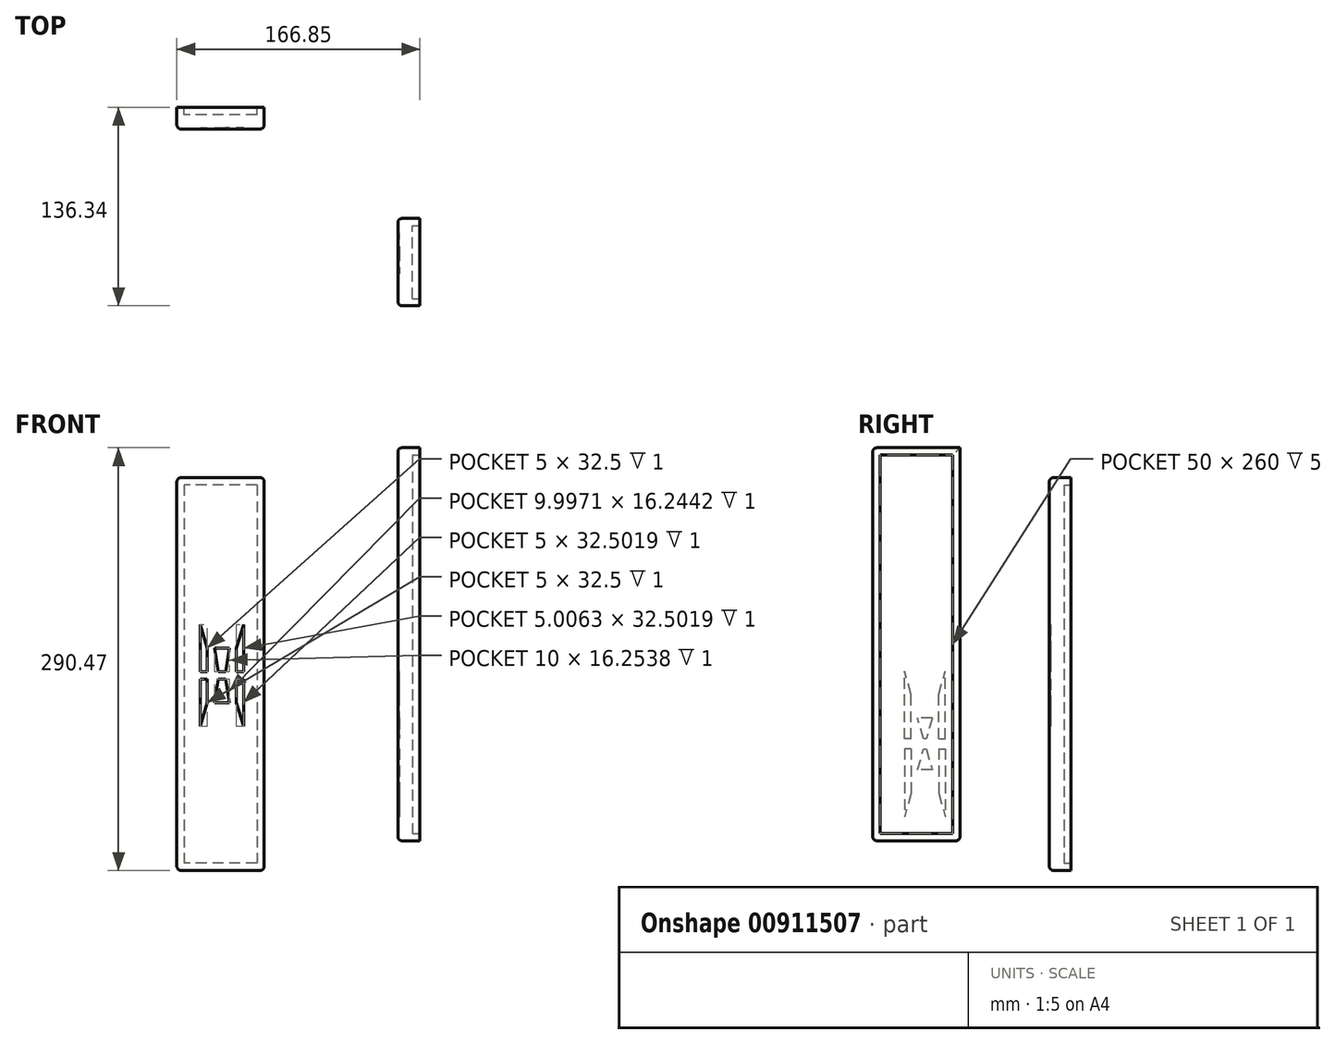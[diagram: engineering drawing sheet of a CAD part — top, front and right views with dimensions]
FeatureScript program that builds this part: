
annotation { "Feature Type Name" : "Feature", "Feature Type Description" : "" }
export const myFeature = defineFeature(function(context is Context, id is Id, definition is map)
    precondition{}
    {
        {
            var Q0;
            Q0=qCreatedBy(makeId("Front.planeOp"),FACE);
            var sketch = newSketch(context, id + "F0", { "sketchPlane" : qUnion([Q0])});
            skPoint(sketch, "E0.middle", {"position": v(0, 0) * mm});
            skLineSegment(sketch, "E1.bottom", {"start": v(-151.85, 109.1) * mm, "end": v(-91.85, 109.1) * mm});
            skLineSegment(sketch, "E1.top", {"start": v(-151.85, -160.9) * mm, "end": v(-91.85, -160.9) * mm});
            skLineSegment(sketch, "E1.left", {"start": v(-151.85, 109.1) * mm, "end": v(-151.85, -160.9) * mm});
            skLineSegment(sketch, "E1.right", {"start": v(-91.85, 109.1) * mm, "end": v(-91.85, -160.9) * mm});
            skSolve(sketch);
        }
        {
            var Q0;
            Q0=qCreatedBy(makeId("Right.planeOp"),FACE);
            var sketch = newSketch(context, id + "F1", { "sketchPlane" : qUnion([Q0])});
            skLineSegment(sketch, "E2.bottom", {"start": v(-136.34, 129.58) * mm, "end": v(-76.34, 129.58) * mm});
            skLineSegment(sketch, "E2.top", {"start": v(-136.34, -140.42) * mm, "end": v(-76.34, -140.42) * mm});
            skLineSegment(sketch, "E2.left", {"start": v(-136.34, 129.58) * mm, "end": v(-136.34, -140.42) * mm});
            skLineSegment(sketch, "E2.right", {"start": v(-76.34, 129.58) * mm, "end": v(-76.34, -140.42) * mm});
            skSolve(sketch);
        }
        {
            var Q0;
            Q0=qSketchRegion(id+"F0",true);
            extrude(context, id + "F2", {"entities" : qUnion([Q0]), "depth" : 15 * mm, "offsetDistance" : 25 * mm});
        }
        {
            var Q0;
            Q0=makeQuery(id+"F0.imprint","IMPRINT",FACE,{"disambiguationData":[TD([[makeQuery(id+"F0.imprint","IMPRINT",EDGE,{"derivedFrom":sQuery(id+"F0.wireOp",EDGE,"E1.bottom")}),-1.0]])]});
            var sketch = newSketch(context, id + "F3", { "sketchPlane" : qUnion([Q0])});
            skLineSegment(sketch, "E3.bottom", {"start": v(-96.85, 104.1) * mm, "end": v(-146.85, 104.1) * mm});
            skLineSegment(sketch, "E3.top", {"start": v(-96.85, -155.9) * mm, "end": v(-146.85, -155.9) * mm});
            skLineSegment(sketch, "E3.left", {"start": v(-96.85, 104.1) * mm, "end": v(-96.85, -155.9) * mm});
            skLineSegment(sketch, "E3.right", {"start": v(-146.85, 104.1) * mm, "end": v(-146.85, -155.9) * mm});
            skSolve(sketch);
        }
        {
            var Q0;
            Q0=makeQuery(id+"F3.imprint","IMPRINT",FACE,{"disambiguationData":[TD([[makeQuery(id+"F3.imprint","IMPRINT",EDGE,{"derivedFrom":sQuery(id+"F3.wireOp",EDGE,"E3.bottom")}),1.0]])]});
            extrude(context, id + "F4", {"entities" : qUnion([Q0]), "operationType" : NewBodyOperationType.ADD, "depth" : -5 * mm, "offsetDistance" : 25 * mm});
        }
        {
            var Q0;
            Q0=qSketchRegion(id+"F1",true);
            extrude(context, id + "F5", {"entities" : qUnion([Q0]), "depth" : 15 * mm, "offsetDistance" : 25 * mm});
        }
        {
            var Q0;
            Q0=makeQuery(id+"F5.opExtrude","CAP_FACE",FACE,{"disambiguationData":[OSD([sQuery(id+"F1.wireOp",EDGE,"E2.bottom"),sQuery(id+"F1.wireOp",EDGE,"E2.top"),sQuery(id+"F1.wireOp",EDGE,"E2.left"),sQuery(id+"F1.wireOp",EDGE,"E2.right")])],"isStart":false});
            var sketch = newSketch(context, id + "F6", { "sketchPlane" : qUnion([Q0])});
            skLineSegment(sketch, "E4.bottom", {"start": v(-131.34, 124.58) * mm, "end": v(-81.34, 124.58) * mm});
            skLineSegment(sketch, "E4.top", {"start": v(-131.34, -135.42) * mm, "end": v(-81.34, -135.42) * mm});
            skLineSegment(sketch, "E4.left", {"start": v(-131.34, 124.58) * mm, "end": v(-131.34, -135.42) * mm});
            skLineSegment(sketch, "E4.right", {"start": v(-81.34, 124.58) * mm, "end": v(-81.34, -135.42) * mm});
            skSolve(sketch);
        }
        {
            var Q0;
            Q0=makeQuery(id+"F6.imprint","IMPRINT",FACE,{"disambiguationData":[TD([[makeQuery(id+"F6.imprint","IMPRINT",EDGE,{"derivedFrom":sQuery(id+"F6.wireOp",EDGE,"E4.bottom")}),-1.0]])]});
            extrude(context, id + "F7", {"entities" : qUnion([Q0]), "operationType" : NewBodyOperationType.REMOVE, "oppositeDirection" : true, "depth" : 5 * mm, "offsetDistance" : 25 * mm});
        }
        {
            var Q0;
            Q0=makeQuery(id+"F4.opExtrude","CAP_FACE",FACE,{"disambiguationData":[OSD([sQuery(id+"F3.wireOp",EDGE,"E3.bottom"),sQuery(id+"F3.wireOp",EDGE,"E3.top"),sQuery(id+"F3.wireOp",EDGE,"E3.left"),sQuery(id+"F3.wireOp",EDGE,"E3.right")])],"isStart":false});
            var sketch = newSketch(context, id + "F8", { "sketchPlane" : qUnion([Q0])});
            skLineSegment(sketch, "E5.bottom", {"start": v(133.85, -150.9) * mm, "end": v(109.85, -150.9) * mm});
            skLineSegment(sketch, "E5.top", {"start": v(133.85, 99.1) * mm, "end": v(109.85, 99.1) * mm});
            skLineSegment(sketch, "E5.left", {"start": v(133.85, -150.9) * mm, "end": v(133.85, 99.1) * mm});
            skLineSegment(sketch, "E5.right", {"start": v(109.85, -150.9) * mm, "end": v(109.85, 99.1) * mm});
            skEllipse(sketch, "E6", {"center": v(121.85, -25.9) * mm, "majorRadius": 25 * mm, "minorRadius": 20 * mm, "majorAxis": v(0, 1)});
            skSolve(sketch);
        }
        {
            var Q0;
            Q0=makeQuery(id+"F8.imprint","IMPRINT",FACE,{"disambiguationData":[TD([[makeQuery(id+"F8.imprint","IMPRINT",EDGE,{"derivedFrom":sQuery(id+"F8.wireOp",EDGE,"E5.bottom")}),-1.0]])]});
            var Q1;
            {var subQ0=sQuery(id+"F8.wireOp",EDGE,"E5.right");var subQ1=sQuery(id+"F8.wireOp",EDGE,"E5.top");var subQ2=makeQuery(id+"F8.imprint","INTERSECT",VERTEX,{"derivedFrom":[subQ1,subQ0]});Q1=makeQuery(id+"F8.imprint","IMPRINT",FACE,{"disambiguationData":[TD([[makeQuery(id+"F8.imprint","IMPRINT",EDGE,{"disambiguationData":[TD([[subQ2,1.0]])],"derivedFrom":subQ1}),1.0]])]});}
            var Q2;
            {var subQ0=sQuery(id+"F8.wireOp",EDGE,"E5.left");var subQ1=sQuery(id+"F8.wireOp",EDGE,"E5.top");var subQ2=makeQuery(id+"F8.imprint","INTERSECT",VERTEX,{"derivedFrom":[subQ1,subQ0]});Q2=makeQuery(id+"F8.imprint","IMPRINT",FACE,{"disambiguationData":[TD([[makeQuery(id+"F8.imprint","IMPRINT",EDGE,{"disambiguationData":[TD([[subQ2,-1.0]])],"derivedFrom":subQ1}),1.0]])]});}
            var Q3;
            {var subQ0=sQuery(id+"F8.wireOp",EDGE,"jjR4p86R-AGvj-MJNc-cVGU-iWlVXVb1kiAX");var subQ1=sQuery(id+"F8.wireOp",EDGE,"E5.right");var subQ2=makeQuery(id+"F8.imprint","INTERSECT",VERTEX,{"derivedFrom":[subQ1,subQ0]});Q3=makeQuery(id+"F8.imprint","IMPRINT",FACE,{"disambiguationData":[TD([[makeQuery(id+"F8.imprint","IMPRINT",EDGE,{"disambiguationData":[TD([[subQ2,-1.0]])],"derivedFrom":subQ1}),-1.0]])]});}
            var Q4;
            {var subQ0=sQuery(id+"F8.wireOp",EDGE,"jjR4p86R-AGvj-MJNc-cVGU-iWlVXVb1kiAX");var subQ1=sQuery(id+"F8.wireOp",EDGE,"E5.left");var subQ2=makeQuery(id+"F8.imprint","INTERSECT",VERTEX,{"derivedFrom":[subQ1,subQ0]});Q4=makeQuery(id+"F8.imprint","IMPRINT",FACE,{"disambiguationData":[TD([[makeQuery(id+"F8.imprint","IMPRINT",EDGE,{"disambiguationData":[TD([[subQ2,-1.0]])],"derivedFrom":subQ1}),1.0]])]});}
            var Q5;
            {var subQ0=sQuery(id+"F8.wireOp",EDGE,"jjR4p86R-AGvj-MJNc-cVGU-iWlVXVb1kiAX");var subQ1=sQuery(id+"F8.wireOp",EDGE,"E5.left");var subQ2=makeQuery(id+"F8.imprint","INTERSECT",VERTEX,{"derivedFrom":[subQ1,subQ0]});Q5=makeQuery(id+"F8.imprint","IMPRINT",FACE,{"disambiguationData":[TD([[makeQuery(id+"F8.imprint","IMPRINT",EDGE,{"disambiguationData":[TD([[subQ2,-1.0]])],"derivedFrom":subQ1}),-1.0]])]});}
            var Q6;
            {var subQ0=sQuery(id+"F8.wireOp",EDGE,"E6");var subQ1=sQuery(id+"F8.wireOp",EDGE,"E5.left");var subQ2=makeQuery(id+"F8.imprint","INTERSECT",VERTEX,{"disambiguationData":[OD(0.0)],"derivedFrom":[subQ1,subQ0]});Q6=makeQuery(id+"F8.imprint","IMPRINT",FACE,{"disambiguationData":[TD([[makeQuery(id+"F8.imprint","IMPRINT",EDGE,{"disambiguationData":[TD([[subQ2,-1.0]])],"derivedFrom":subQ1}),-1.0]])]});}
            var Q7;
            {var subQ0=sQuery(id+"F8.wireOp",EDGE,"E6");var subQ1=sQuery(id+"F8.wireOp",EDGE,"E5.left");var subQ2=makeQuery(id+"F8.imprint","INTERSECT",VERTEX,{"disambiguationData":[OD(0.0)],"derivedFrom":[subQ1,subQ0]});Q7=makeQuery(id+"F8.imprint","IMPRINT",FACE,{"disambiguationData":[TD([[makeQuery(id+"F8.imprint","IMPRINT",EDGE,{"disambiguationData":[TD([[subQ2,-1.0]])],"derivedFrom":subQ1}),1.0]])]});}
            var Q8;
            {var subQ0=sQuery(id+"F8.wireOp",EDGE,"E6");var subQ1=sQuery(id+"F8.wireOp",EDGE,"E5.right");var subQ2=makeQuery(id+"F8.imprint","INTERSECT",VERTEX,{"disambiguationData":[OD(0.0)],"derivedFrom":[subQ1,subQ0]});Q8=makeQuery(id+"F8.imprint","IMPRINT",FACE,{"disambiguationData":[TD([[makeQuery(id+"F8.imprint","IMPRINT",EDGE,{"disambiguationData":[TD([[subQ2,-1.0]])],"derivedFrom":subQ1}),-1.0]])]});}
            var Q9;
            {var subQ0=sQuery(id+"F8.wireOp",EDGE,"E6");var subQ1=sQuery(id+"F8.wireOp",EDGE,"E5.right");var subQ2=makeQuery(id+"F8.imprint","INTERSECT",VERTEX,{"disambiguationData":[OD(0.0)],"derivedFrom":[subQ1,subQ0]});Q9=makeQuery(id+"F8.imprint","IMPRINT",FACE,{"disambiguationData":[TD([[makeQuery(id+"F8.imprint","IMPRINT",EDGE,{"disambiguationData":[TD([[subQ2,-1.0]])],"derivedFrom":subQ1}),1.0]])]});}
            var Q10;
            {var subQ0=sQuery(id+"F8.wireOp",EDGE,"jjR4p86R-AGvj-MJNc-cVGU-iWlVXVb1kiAX");var subQ1=sQuery(id+"F8.wireOp",EDGE,"E5.right");var subQ2=makeQuery(id+"F8.imprint","INTERSECT",VERTEX,{"derivedFrom":[subQ1,subQ0]});Q10=makeQuery(id+"F8.imprint","IMPRINT",FACE,{"disambiguationData":[TD([[makeQuery(id+"F8.imprint","IMPRINT",EDGE,{"disambiguationData":[TD([[subQ2,-1.0]])],"derivedFrom":subQ1}),1.0]])]});}
            extrude(context, id + "F9", {"entities" : qUnion([Q0, Q1, Q2, Q3, Q4, Q5, Q6, Q7, Q8, Q9, Q10]), "operationType" : NewBodyOperationType.REMOVE, "oppositeDirection" : true, "depth" : 10 * mm, "offsetDistance" : 25 * mm});
        }
        {
            var Q0;
            Q0=makeQuery(id+"F2.opExtrude","CAP_EDGE",EDGE,{"disambiguationData":[OSD([sQuery(id+"F0.wireOp",EDGE,"E1.bottom")])],"isStart":false});
            var Q1;
            Q1=makeQuery(id+"F2.opExtrude","SWEPT_EDGE",EDGE,{"disambiguationData":[OSD([sQuery(id+"F0.wireOp",EDGE,"E1.bottom"),sQuery(id+"F0.wireOp",EDGE,"E1.left")])]});
            var Q2;
            Q2=makeQuery(id+"F2.opExtrude","SWEPT_EDGE",EDGE,{"disambiguationData":[OSD([sQuery(id+"F0.wireOp",EDGE,"E1.bottom"),sQuery(id+"F0.wireOp",EDGE,"E1.right")])]});
            var Q3;
            Q3=makeQuery(id+"F2.opExtrude","CAP_EDGE",EDGE,{"disambiguationData":[OSD([sQuery(id+"F0.wireOp",EDGE,"E1.right")])],"isStart":false});
            var Q4;
            Q4=makeQuery(id+"F2.opExtrude","CAP_EDGE",EDGE,{"disambiguationData":[OSD([sQuery(id+"F0.wireOp",EDGE,"E1.left")])],"isStart":false});
            var Q5;
            Q5=makeQuery(id+"F2.opExtrude","CAP_EDGE",EDGE,{"disambiguationData":[OSD([sQuery(id+"F0.wireOp",EDGE,"E1.top")])],"isStart":false});
            var Q6;
            Q6=makeQuery(id+"F2.opExtrude","SWEPT_EDGE",EDGE,{"disambiguationData":[OSD([sQuery(id+"F0.wireOp",EDGE,"E1.top"),sQuery(id+"F0.wireOp",EDGE,"E1.left")])]});
            var Q7;
            Q7=makeQuery(id+"F2.opExtrude","SWEPT_EDGE",EDGE,{"disambiguationData":[OSD([sQuery(id+"F0.wireOp",EDGE,"E1.top"),sQuery(id+"F0.wireOp",EDGE,"E1.right")])]});
            fillet(context, id + "F10", {"entities" : qUnion([Q0, Q1, Q2, Q3, Q4, Q5, Q6, Q7]), "radius" : 3 * mm, "tangentPropagation" : true, "allowEdgeOverflow" : false});
        }
        {
            var Q0;
            Q0=makeQuery(id+"F5.opExtrude","SWEPT_EDGE",EDGE,{"disambiguationData":[OSD([sQuery(id+"F1.wireOp",EDGE,"E2.bottom"),sQuery(id+"F1.wireOp",EDGE,"E2.left")])]});
            var Q1;
            Q1=makeQuery(id+"F5.opExtrude","CAP_EDGE",EDGE,{"disambiguationData":[OSD([sQuery(id+"F1.wireOp",EDGE,"E2.bottom")])],"isStart":true});
            var Q2;
            Q2=makeQuery(id+"F5.opExtrude","CAP_EDGE",EDGE,{"disambiguationData":[OSD([sQuery(id+"F1.wireOp",EDGE,"E2.left")])],"isStart":true});
            var Q3;
            Q3=makeQuery(id+"F5.opExtrude","CAP_EDGE",EDGE,{"disambiguationData":[OSD([sQuery(id+"F1.wireOp",EDGE,"E2.right")])],"isStart":true});
            var Q4;
            Q4=makeQuery(id+"F5.opExtrude","CAP_EDGE",EDGE,{"disambiguationData":[OSD([sQuery(id+"F1.wireOp",EDGE,"E2.top")])],"isStart":true});
            var Q5;
            Q5=makeQuery(id+"F5.opExtrude","SWEPT_EDGE",EDGE,{"disambiguationData":[OSD([sQuery(id+"F1.wireOp",EDGE,"E2.top"),sQuery(id+"F1.wireOp",EDGE,"E2.right")])]});
            var Q6;
            Q6=makeQuery(id+"F5.opExtrude","SWEPT_EDGE",EDGE,{"disambiguationData":[OSD([sQuery(id+"F1.wireOp",EDGE,"E2.top"),sQuery(id+"F1.wireOp",EDGE,"E2.left")])]});
            fillet(context, id + "F11", {"entities" : qUnion([Q0, Q1, Q2, Q3, Q4, Q5, Q6]), "radius" : 3 * mm, "tangentPropagation" : true, "allowEdgeOverflow" : false});
        }
        {
            var Q0;
            Q0=makeQuery(id+"F5.opExtrude","CAP_FACE",FACE,{"disambiguationData":[OSD([sQuery(id+"F1.wireOp",EDGE,"E2.bottom"),sQuery(id+"F1.wireOp",EDGE,"E2.top"),sQuery(id+"F1.wireOp",EDGE,"E2.left"),sQuery(id+"F1.wireOp",EDGE,"E2.right")])],"isStart":true});
            var sketch = newSketch(context, id + "F12", { "sketchPlane" : qUnion([Q0])});
            skLineSegment(sketch, "E7", {"start": v(95.46, -56.01) * mm, "end": v(105.46, -56.01) * mm});
            skLineSegment(sketch, "E8", {"start": v(95.46, -91.72) * mm, "end": v(105.46, -91.72) * mm});
            skLineSegment(sketch, "E9", {"start": v(90.96, -39.94) * mm, "end": v(86.46, -23.87) * mm});
            skLineSegment(sketch, "E10", {"start": v(90.96, -107.8) * mm, "end": v(86.46, -123.87) * mm});
            skLineSegment(sketch, "E11", {"start": v(109.96, -107.8) * mm, "end": v(114.46, -123.87) * mm});
            skLineSegment(sketch, "E12", {"start": v(109.96, -39.94) * mm, "end": v(114.46, -23.87) * mm});
            skLineSegment(sketch, "E13", {"start": v(95.46, -56.01) * mm, "end": v(99.5, -70.46) * mm});
            skLineSegment(sketch, "E14", {"start": v(99.5, -70.46) * mm, "end": v(101.41, -70.46) * mm});
            skLineSegment(sketch, "E15", {"start": v(101.41, -70.46) * mm, "end": v(105.46, -56.01) * mm});
            skLineSegment(sketch, "E16", {"start": v(105.46, -91.72) * mm, "end": v(101.41, -77.27) * mm});
            skLineSegment(sketch, "E17", {"start": v(101.41, -77.27) * mm, "end": v(99.5, -77.27) * mm});
            skLineSegment(sketch, "E18", {"start": v(99.5, -77.27) * mm, "end": v(95.46, -91.72) * mm});
            skLineSegment(sketch, "E19", {"start": v(90.96, -77.27) * mm, "end": v(86.46, -77.27) * mm});
            skLineSegment(sketch, "E20", {"start": v(109.96, -77.27) * mm, "end": v(114.46, -77.27) * mm});
            skLineSegment(sketch, "E21", {"start": v(109.96, -70.46) * mm, "end": v(114.46, -70.46) * mm});
            skLineSegment(sketch, "E22", {"start": v(109.96, -70.46) * mm, "end": v(109.96, -39.94) * mm});
            skLineSegment(sketch, "E23", {"start": v(109.96, -77.27) * mm, "end": v(109.96, -107.8) * mm});
            skLineSegment(sketch, "E24", {"start": v(90.96, -70.46) * mm, "end": v(86.46, -70.46) * mm});
            skLineSegment(sketch, "E25", {"start": v(90.96, -70.46) * mm, "end": v(90.96, -39.94) * mm});
            skLineSegment(sketch, "E26", {"start": v(90.96, -77.27) * mm, "end": v(90.96, -107.8) * mm});
            skLineSegment(sketch, "E27", {"start": v(86.46, -70.46) * mm, "end": v(86.46, -23.87) * mm});
            skLineSegment(sketch, "E28", {"start": v(86.46, -77.27) * mm, "end": v(86.46, -123.87) * mm});
            skLineSegment(sketch, "E29", {"start": v(114.46, -70.46) * mm, "end": v(114.46, -23.87) * mm});
            skLineSegment(sketch, "E30", {"start": v(114.46, -77.27) * mm, "end": v(114.46, -123.87) * mm});
            skSolve(sketch);
        }
        {
            var Q0;
            Q0=makeQuery(id+"F12.imprint","IMPRINT",FACE,{"disambiguationData":[TD([[makeQuery(id+"F12.imprint","IMPRINT",EDGE,{"derivedFrom":sQuery(id+"F12.wireOp",EDGE,"E7")}),-1.0]])]});
            var Q1;
            Q1=makeQuery(id+"F12.imprint","IMPRINT",FACE,{"disambiguationData":[TD([[makeQuery(id+"F12.imprint","IMPRINT",EDGE,{"derivedFrom":sQuery(id+"F12.wireOp",EDGE,"E9")}),1.0]])]});
            var Q2;
            Q2=makeQuery(id+"F12.imprint","IMPRINT",FACE,{"disambiguationData":[TD([[makeQuery(id+"F12.imprint","IMPRINT",EDGE,{"derivedFrom":sQuery(id+"F12.wireOp",EDGE,"E12")}),-1.0]])]});
            var Q3;
            Q3=makeQuery(id+"F12.imprint","IMPRINT",FACE,{"disambiguationData":[TD([[makeQuery(id+"F12.imprint","IMPRINT",EDGE,{"derivedFrom":sQuery(id+"F12.wireOp",EDGE,"E11")}),1.0]])]});
            var Q4;
            Q4=makeQuery(id+"F12.imprint","IMPRINT",FACE,{"disambiguationData":[TD([[makeQuery(id+"F12.imprint","IMPRINT",EDGE,{"derivedFrom":sQuery(id+"F12.wireOp",EDGE,"E8")}),1.0]])]});
            var Q5;
            Q5=makeQuery(id+"F12.imprint","IMPRINT",FACE,{"disambiguationData":[TD([[makeQuery(id+"F12.imprint","IMPRINT",EDGE,{"derivedFrom":sQuery(id+"F12.wireOp",EDGE,"E10")}),-1.0]])]});
            extrude(context, id + "F13", {"entities" : qUnion([Q0, Q1, Q2, Q3, Q4, Q5]), "operationType" : NewBodyOperationType.REMOVE, "oppositeDirection" : true, "depth" : 1 * mm, "offsetDistance" : 25 * mm});
        }
        {
            var Q0;
            Q0=makeQuery(id+"F2.opExtrude","CAP_FACE",FACE,{"disambiguationData":[OSD([sQuery(id+"F0.wireOp",EDGE,"E1.bottom"),sQuery(id+"F0.wireOp",EDGE,"E1.top"),sQuery(id+"F0.wireOp",EDGE,"E1.left"),sQuery(id+"F0.wireOp",EDGE,"E1.right")])],"isStart":false});
            var sketch = newSketch(context, id + "F14", { "sketchPlane" : qUnion([Q0])});
            skLineSegment(sketch, "E31", {"start": v(-135.9, -24.37) * mm, "end": v(-130.9, -24.37) * mm});
            skLineSegment(sketch, "E32", {"start": v(-130.9, -24.37) * mm, "end": v(-130.9, -8.12) * mm});
            skLineSegment(sketch, "E33", {"start": v(-130.9, -8.12) * mm, "end": v(-135.9, 8.13) * mm});
            skLineSegment(sketch, "E34", {"start": v(-125.9, -8.12) * mm, "end": v(-120.9, -8.12) * mm});
            skLineSegment(sketch, "E35", {"start": v(-120.9, -8.12) * mm, "end": v(-115.9, -8.12) * mm});
            skLineSegment(sketch, "E36", {"start": v(-125.9, -8.12) * mm, "end": v(-115.9, -8.12) * mm});
            skLineSegment(sketch, "E37", {"start": v(-110.9, -8.12) * mm, "end": v(-110.9, -24.37) * mm});
            skLineSegment(sketch, "E38", {"start": v(-110.9, -24.37) * mm, "end": v(-105.9, -24.37) * mm});
            skLineSegment(sketch, "E39", {"start": v(-105.9, -24.37) * mm, "end": v(-105.9, 8.13) * mm});
            skLineSegment(sketch, "E40", {"start": v(-105.9, 8.13) * mm, "end": v(-110.9, -8.12) * mm});
            skLineSegment(sketch, "E41", {"start": v(-135.9, 8.13) * mm, "end": v(-135.9, -24.37) * mm});
            skLineSegment(sketch, "E42.MirrorCS", {"start": v(-110.9, -24.38) * mm, "end": v(-105.9, -24.38) * mm});
            skLineSegment(sketch, "E43", {"start": v(-135.9, -29.37) * mm, "end": v(-135.9, -61.87) * mm});
            skLineSegment(sketch, "E44", {"start": v(-135.9, -29.37) * mm, "end": v(-135.9, -45.62) * mm});
            skLineSegment(sketch, "E45", {"start": v(-135.9, -29.37) * mm, "end": v(-130.9, -29.37) * mm});
            skLineSegment(sketch, "E46", {"start": v(-130.9, -29.37) * mm, "end": v(-130.9, -45.62) * mm});
            skLineSegment(sketch, "E47", {"start": v(-130.9, -45.62) * mm, "end": v(-135.9, -61.87) * mm});
            skLineSegment(sketch, "E48", {"start": v(-110.9, -29.38) * mm, "end": v(-110.9, -45.63) * mm});
            skLineSegment(sketch, "E49", {"start": v(-105.9, -29.38) * mm, "end": v(-105.9, -61.88) * mm});
            skLineSegment(sketch, "E50", {"start": v(-105.9, -61.88) * mm, "end": v(-110.9, -45.63) * mm});
            skLineSegment(sketch, "E51", {"start": v(-125.9, -45.62) * mm, "end": v(-115.9, -45.62) * mm});
            skLineSegment(sketch, "E52", {"start": v(-110.9, -29.38) * mm, "end": v(-105.9, -29.38) * mm});
            skLineSegment(sketch, "E53", {"start": v(-123.4, -24.37) * mm, "end": v(-118.4, -24.37) * mm});
            skLineSegment(sketch, "E54", {"start": v(-125.9, -8.12) * mm, "end": v(-123.4, -24.37) * mm});
            skLineSegment(sketch, "E55", {"start": v(-115.9, -8.12) * mm, "end": v(-118.4, -24.37) * mm});
            skLineSegment(sketch, "E56.MirrorCS", {"start": v(-125.9, -45.63) * mm, "end": v(-123.4, -29.37) * mm});
            skLineSegment(sketch, "E57.MirrorCS", {"start": v(-123.4, -29.37) * mm, "end": v(-118.4, -29.37) * mm});
            skLineSegment(sketch, "E58.MirrorCS", {"start": v(-115.9, -45.63) * mm, "end": v(-118.4, -29.37) * mm});
            skSolve(sketch);
        }
        {
            var Q0;
            Q0 = qSketchRegion(id + "F14", true);
            extrude(context, id + "F15", {"entities" : qUnion([Q0]), "operationType" : NewBodyOperationType.REMOVE, "oppositeDirection" : true, "depth" : 1 * mm, "offsetDistance" : 25 * mm});
        }
    });
